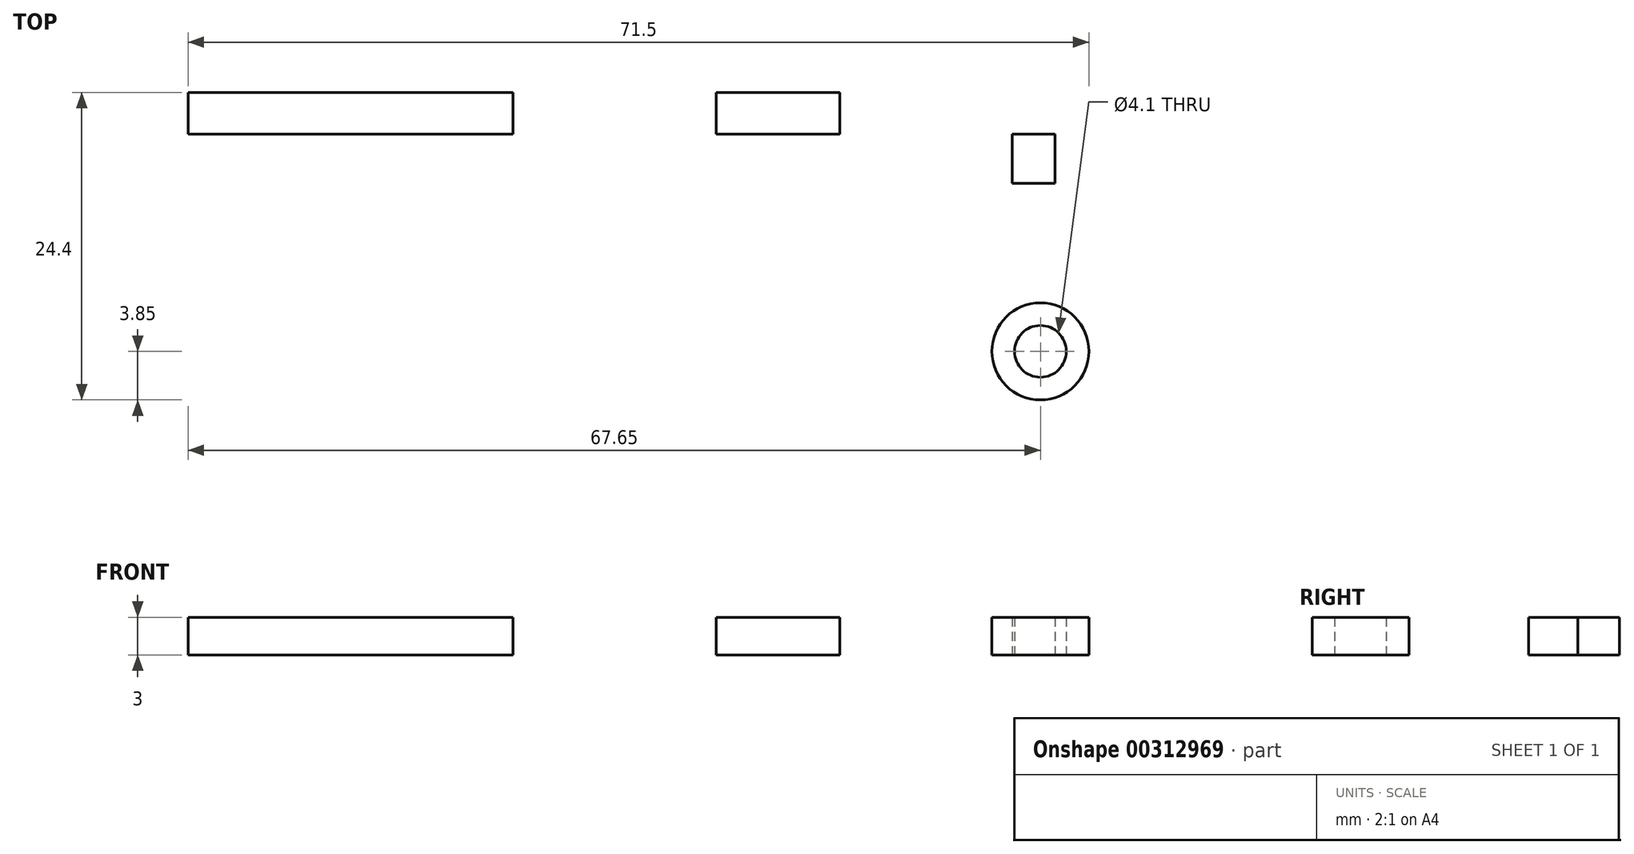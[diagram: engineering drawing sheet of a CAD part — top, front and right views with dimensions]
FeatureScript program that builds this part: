
annotation { "Feature Type Name" : "Feature", "Feature Type Description" : "" }
export const myFeature = defineFeature(function(context is Context, id is Id, definition is map)
    precondition{}
    {
        {
            var Q0;
            Q0=qCreatedBy(makeId("Top.planeOp"),FACE);
            var sketch = newSketch(context, id + "F0", { "sketchPlane" : qUnion([Q0])});
            skLineSegment(sketch, "E0.bottom", {"start": v(34.4, 9.65) * mm, "end": v(-34.4, 9.65) * mm});
            skLineSegment(sketch, "E0.top", {"start": v(34.4, -9.65) * mm, "end": v(-34.4, -9.65) * mm});
            skLineSegment(sketch, "E0.left", {"start": v(34.4, 9.65) * mm, "end": v(34.41, -9.65) * mm});
            skLineSegment(sketch, "E0.right", {"start": v(-34.4, 9.65) * mm, "end": v(-34.4, -9.65) * mm});
            skPoint(sketch, "E0.middle", {"position": v(0, 0) * mm});
            skLineSegment(sketch, "E1.bottom", {"start": v(34.4, 9.65) * mm, "end": v(31, 9.65) * mm});
            skLineSegment(sketch, "E1.top", {"start": v(34.4, 6.35) * mm, "end": v(31, 6.35) * mm});
            skLineSegment(sketch, "E1.left", {"start": v(34.4, 9.65) * mm, "end": v(34.4, 6.35) * mm});
            skLineSegment(sketch, "E1.right", {"start": v(31, 9.65) * mm, "end": v(31, 6.35) * mm});
            skLineSegment(sketch, "E2.bottom", {"start": v(34.4, -9.65) * mm, "end": v(31, -9.65) * mm});
            skLineSegment(sketch, "E2.top", {"start": v(34.4, -6.35) * mm, "end": v(31.01, -6.35) * mm});
            skLineSegment(sketch, "E2.left", {"start": v(34.4, -9.65) * mm, "end": v(34.4, -6.35) * mm});
            skLineSegment(sketch, "E2.right", {"start": v(31, -9.65) * mm, "end": v(31, -6.35) * mm});
            skCircle(sketch, "E3", {"center": v(33.24, -10.9) * mm, "radius": 2.05 * mm});
            skCircle(sketch, "E4", {"center": v(33.24, -10.9) * mm, "radius": 3.85 * mm});
            skLineSegment(sketch, "E5.left", {"start": v(34.4, 6.35) * mm, "end": v(34.4, -9.65) * mm});
            skLineSegment(sketch, "E5.right", {"start": v(31, 6.35) * mm, "end": v(31, -9.65) * mm});
            skLineSegment(sketch, "E6.bottom", {"start": v(31, -1.65) * mm, "end": v(25, -1.65) * mm});
            skLineSegment(sketch, "E6.top", {"start": v(31, -0.25) * mm, "end": v(25, -0.25) * mm});
            skLineSegment(sketch, "E6.left", {"start": v(31, -1.65) * mm, "end": v(31, -0.25) * mm});
            skLineSegment(sketch, "E6.right", {"start": v(25, -1.65) * mm, "end": v(25, -0.25) * mm});
            skLineSegment(sketch, "E7.top", {"start": v(31, -3.05) * mm, "end": v(25, -3.05) * mm});
            skLineSegment(sketch, "E7.left", {"start": v(31, -1.65) * mm, "end": v(31, -3.05) * mm});
            skLineSegment(sketch, "E7.right", {"start": v(25, -1.65) * mm, "end": v(25, -3.05) * mm});
            skLineSegment(sketch, "E8.bottom", {"start": v(29.26, 0.35) * mm, "end": v(26.76, 0.35) * mm});
            skLineSegment(sketch, "E8.top", {"start": v(29.26, -3.65) * mm, "end": v(26.76, -3.65) * mm});
            skLineSegment(sketch, "E8.left", {"start": v(29.26, 0.35) * mm, "end": v(29.26, -3.65) * mm});
            skLineSegment(sketch, "E8.right", {"start": v(26.76, 0.35) * mm, "end": v(26.76, -3.65) * mm});
            skPoint(sketch, "E8.middle", {"position": v(28, -1.65) * mm});
            skLineSegment(sketch, "E9.bottom", {"start": v(34.4, 6.35) * mm, "end": v(17.31, 6.35) * mm});
            skLineSegment(sketch, "E9.top", {"start": v(34.4, 9.65) * mm, "end": v(17.31, 9.65) * mm});
            skLineSegment(sketch, "E9.left", {"start": v(34.4, 6.35) * mm, "end": v(34.4, 9.65) * mm});
            skLineSegment(sketch, "E9.right", {"start": v(17.31, 6.35) * mm, "end": v(17.31, 9.65) * mm});
            skLineSegment(sketch, "E10.bottom", {"start": v(-34.4, 6.35) * mm, "end": v(-18.4, 6.35) * mm});
            skLineSegment(sketch, "E10.top", {"start": v(-34.4, 9.65) * mm, "end": v(-18.4, 9.65) * mm});
            skLineSegment(sketch, "E10.left", {"start": v(-34.4, 6.35) * mm, "end": v(-34.4, 9.65) * mm});
            skLineSegment(sketch, "E10.right", {"start": v(-18.4, 6.35) * mm, "end": v(-18.4, 9.65) * mm});
            skLineSegment(sketch, "E11.bottom", {"start": v(-18.4, 6.35) * mm, "end": v(-8.6, 6.35) * mm});
            skLineSegment(sketch, "E11.top", {"start": v(-18.4, 9.65) * mm, "end": v(-8.6, 9.65) * mm});
            skLineSegment(sketch, "E11.right", {"start": v(-8.6, 6.35) * mm, "end": v(-8.6, 9.65) * mm});
            skLineSegment(sketch, "E12.bottom", {"start": v(17.31, 6.35) * mm, "end": v(7.5, 6.35) * mm});
            skLineSegment(sketch, "E12.top", {"start": v(17.31, 9.65) * mm, "end": v(7.5, 9.65) * mm});
            skLineSegment(sketch, "E12.right", {"start": v(7.5, 6.35) * mm, "end": v(7.5, 9.65) * mm});
            skLineSegment(sketch, "E13", {"start": v(-8.6, 6.35) * mm, "end": v(7.5, 6.35) * mm});
            skLineSegment(sketch, "E14.bottom", {"start": v(0, 6.35) * mm, "end": v(1.4, 6.35) * mm});
            skLineSegment(sketch, "E14.top", {"start": v(0, 0.35) * mm, "end": v(1.4, 0.35) * mm});
            skLineSegment(sketch, "E14.left", {"start": v(0, 6.35) * mm, "end": v(0, 0.35) * mm});
            skLineSegment(sketch, "E14.right", {"start": v(1.4, 6.35) * mm, "end": v(1.4, 0.35) * mm});
            skLineSegment(sketch, "E15.bottom", {"start": v(0, 6.35) * mm, "end": v(-1.4, 6.35) * mm});
            skLineSegment(sketch, "E15.top", {"start": v(0, 0.35) * mm, "end": v(-1.4, 0.35) * mm});
            skLineSegment(sketch, "E15.right", {"start": v(-1.4, 6.35) * mm, "end": v(-1.4, 0.35) * mm});
            skLineSegment(sketch, "E16.bottom", {"start": v(2, 4.6) * mm, "end": v(-2, 4.6) * mm});
            skLineSegment(sketch, "E16.top", {"start": v(2, 2.1) * mm, "end": v(-2, 2.1) * mm});
            skLineSegment(sketch, "E16.left", {"start": v(2, 4.6) * mm, "end": v(2, 2.1) * mm});
            skLineSegment(sketch, "E16.right", {"start": v(-2, 4.6) * mm, "end": v(-2, 2.1) * mm});
            skPoint(sketch, "E16.middle", {"position": v(0, 3.35) * mm});
            skLineSegment(sketch, "E17.top", {"start": v(34.4, 2.45) * mm, "end": v(31, 2.45) * mm});
            skLineSegment(sketch, "E17.left", {"start": v(34.4, 6.35) * mm, "end": v(34.4, 2.45) * mm});
            skLineSegment(sketch, "E17.right", {"start": v(31, 6.35) * mm, "end": v(31, 2.45) * mm});
            skSolve(sketch);
        }
        {
            var Q0;
            {var subQ24=sQuery(id+"F0.wireOp",EDGE,"E0.right");Q0=makeQuery(id+"F0.imprint","IMPRINT",FACE,{"disambiguationData":[TD([[makeQuery(id+"F0.imprint","IMPRINT",EDGE,{"derivedFrom":subQ24}),1.0]])]});}
            var Q1;
            Q1=makeQuery(id+"F0.imprint","IMPRINT",FACE,{"disambiguationData":[TD([[makeQuery(id+"F0.imprint","IMPRINT",EDGE,{"derivedFrom":sQuery(id+"F0.wireOp",EDGE,"E1.top")}),1.0]])]});
            var Q2;
            Q2=makeQuery(id+"F0.imprint","IMPRINT",FACE,{"disambiguationData":[TD([[makeQuery(id+"F0.imprint","IMPRINT",EDGE,{"derivedFrom":sQuery(id+"F0.wireOp",EDGE,"E12.bottom")}),-1.0]])]});
            var Q3;
            Q3=makeQuery(id+"F0.imprint","IMPRINT",FACE,{"disambiguationData":[TD([[makeQuery(id+"F0.imprint","IMPRINT",EDGE,{"derivedFrom":sQuery(id+"F0.wireOp",EDGE,"E11.bottom")}),1.0]])]});
            var Q4;
            {var subQ3=sQuery(id+"F0.wireOp",EDGE,"E3");var subQ6=sQuery(id+"F0.wireOp",EDGE,"E2.bottom");var subQ8=makeQuery(id+"F0.imprint","INTERSECT",VERTEX,{"derivedFrom":[subQ3,subQ6]});Q4=makeQuery(id+"F0.imprint","IMPRINT",FACE,{"disambiguationData":[TD([[makeQuery(id+"F0.imprint","IMPRINT",EDGE,{"disambiguationData":[TD([[subQ8,1.0]])],"derivedFrom":subQ3}),-1.0]])]});}
            var Q5;
            {var subQ1=sQuery(id+"F0.wireOp",EDGE,"E0.top");var subQ3=sQuery(id+"F0.wireOp",EDGE,"E4");var subQ4=makeQuery(id+"F0.imprint","INTERSECT",VERTEX,{"derivedFrom":[subQ1,subQ3]});Q5=makeQuery(id+"F0.imprint","IMPRINT",FACE,{"disambiguationData":[TD([[makeQuery(id+"F0.imprint","IMPRINT",EDGE,{"disambiguationData":[TD([[subQ4,1.0]])],"derivedFrom":subQ3}),1.0]])]});}
            var Q6;
            {var subQ5=sQuery(id+"F0.wireOp",EDGE,"E2.bottom");var subQ7=sQuery(id+"F0.wireOp",EDGE,"E3");var subQ8=makeQuery(id+"F0.imprint","INTERSECT",VERTEX,{"derivedFrom":[subQ7,subQ5]});Q6=makeQuery(id+"F0.imprint","IMPRINT",FACE,{"disambiguationData":[TD([[makeQuery(id+"F0.imprint","IMPRINT",EDGE,{"disambiguationData":[TD([[subQ8,-1.0]])],"derivedFrom":subQ7}),-1.0]])]});}
            extrude(context, id + "F1", {"entities" : qUnion([Q0, Q1, Q2, Q3, Q4, Q5, Q6]), "depth" : 3 * mm});
        }
    });
